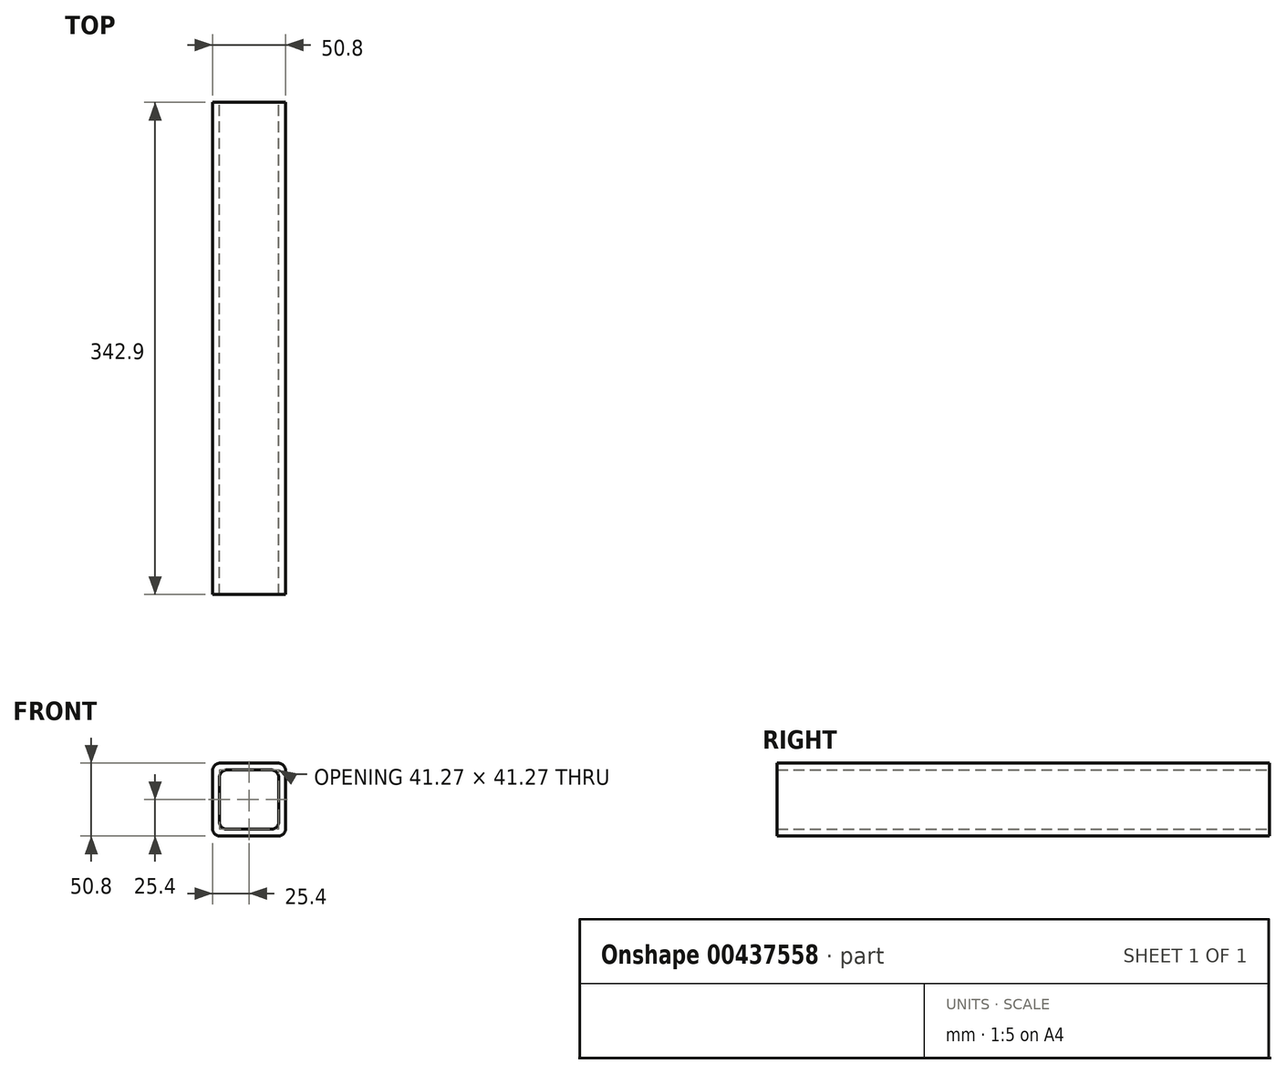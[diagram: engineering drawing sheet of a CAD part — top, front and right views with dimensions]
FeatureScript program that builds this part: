
annotation { "Feature Type Name" : "Feature", "Feature Type Description" : "" }
export const myFeature = defineFeature(function(context is Context, id is Id, definition is map)
    precondition{}
    {
        {
            var Q0;
            Q0=qCreatedBy(makeId("Front.planeOp"),FACE);
            var sketch = newSketch(context, id + "F0", { "sketchPlane" : qUnion([Q0])});
            skLineSegment(sketch, "E0.bottom", {"start": v(25.4, 25.4) * mm, "end": v(-25.4, 25.4) * mm});
            skLineSegment(sketch, "E0.top", {"start": v(25.4, -25.4) * mm, "end": v(-25.4, -25.4) * mm});
            skLineSegment(sketch, "E0.left", {"start": v(25.4, 25.4) * mm, "end": v(25.4, -25.4) * mm});
            skLineSegment(sketch, "E0.right", {"start": v(-25.4, 25.4) * mm, "end": v(-25.4, -25.4) * mm});
            skPoint(sketch, "E0.middle", {"position": v(0, 0) * mm});
            skLineSegment(sketch, "E1.bottom", {"start": v(20.64, -20.64) * mm, "end": v(-20.64, -20.64) * mm});
            skLineSegment(sketch, "E1.top", {"start": v(20.64, 20.64) * mm, "end": v(-20.64, 20.64) * mm});
            skLineSegment(sketch, "E1.left", {"start": v(20.64, -20.64) * mm, "end": v(20.64, 20.64) * mm});
            skLineSegment(sketch, "E1.right", {"start": v(-20.64, -20.64) * mm, "end": v(-20.64, 20.64) * mm});
            skSolve(sketch);
        }
        {
            var Q0;
            Q0 = qSketchRegion(id + "F0", true);
            extrude(context, id + "F1", {"entities" : qUnion([Q0]), "endBound" : BoundingType.SYMMETRIC, "depth" : 342.9 * mm});
        }
        {
            var Q0;
            Q0=makeQuery(id+"F1.opExtrude","SWEPT_EDGE",EDGE,{"disambiguationData":[OSD([sQuery(id+"F0.wireOp",EDGE,"E1.top"),sQuery(id+"F0.wireOp",EDGE,"E1.right")])]});
            var Q1;
            Q1=makeQuery(id+"F1.opExtrude","SWEPT_EDGE",EDGE,{"disambiguationData":[OSD([sQuery(id+"F0.wireOp",EDGE,"E0.top"),sQuery(id+"F0.wireOp",EDGE,"E0.right")])]});
            var Q2;
            Q2=makeQuery(id+"F1.opExtrude","SWEPT_EDGE",EDGE,{"disambiguationData":[OSD([sQuery(id+"F0.wireOp",EDGE,"E0.top"),sQuery(id+"F0.wireOp",EDGE,"E0.left")])]});
            var Q3;
            Q3=makeQuery(id+"F1.opExtrude","SWEPT_EDGE",EDGE,{"disambiguationData":[OSD([sQuery(id+"F0.wireOp",EDGE,"E1.top"),sQuery(id+"F0.wireOp",EDGE,"E1.left")])]});
            var Q4;
            Q4=makeQuery(id+"F1.opExtrude","SWEPT_EDGE",EDGE,{"disambiguationData":[OSD([sQuery(id+"F0.wireOp",EDGE,"E0.bottom"),sQuery(id+"F0.wireOp",EDGE,"E0.left")])]});
            var Q5;
            Q5=makeQuery(id+"F1.opExtrude","SWEPT_EDGE",EDGE,{"disambiguationData":[OSD([sQuery(id+"F0.wireOp",EDGE,"E0.bottom"),sQuery(id+"F0.wireOp",EDGE,"E0.right")])]});
            fillet(context, id + "F2", {"entities" : qUnion([Q0, Q1, Q2, Q3, Q4, Q5]), "radius" : 5.08 * mm, "tangentPropagation" : true, "allowEdgeOverflow" : false});
        }
        {
            var Q0;
            Q0=makeQuery(id+"F1.opExtrude","SWEPT_EDGE",EDGE,{"disambiguationData":[OSD([sQuery(id+"F0.wireOp",EDGE,"E1.bottom"),sQuery(id+"F0.wireOp",EDGE,"E1.right")])]});
            var Q1;
            Q1=makeQuery(id+"F1.opExtrude","SWEPT_EDGE",EDGE,{"disambiguationData":[OSD([sQuery(id+"F0.wireOp",EDGE,"E1.bottom"),sQuery(id+"F0.wireOp",EDGE,"E1.left")])]});
            fillet(context, id + "F3", {"entities" : qUnion([Q0, Q1]), "radius" : 5.08 * mm, "tangentPropagation" : true, "allowEdgeOverflow" : false});
        }
    });
